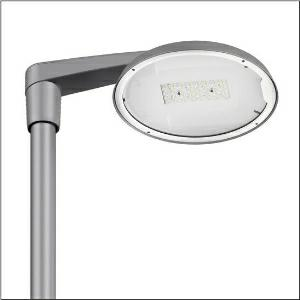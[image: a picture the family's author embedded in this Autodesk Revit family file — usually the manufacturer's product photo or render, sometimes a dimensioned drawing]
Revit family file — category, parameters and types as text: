
# Revit family: dl_r__50_iq_mini___st0_5a_5xa248b41f08je_3ec1
name_source: partatom
category: Lighting Fixtures
units: mm (PartAtom-declared; Revit-internal decimal feet)

## family parameters
Cut with Voids When Loaded = No
Host = Face
Light Source = No
Part Type = Normal
Room Calculation Point = No
Round Connector Dimension = Use Diameter
Shared = No

## types (1)
- --- (1 x LED, 10300 lm, 62.6 W, 4000K)
    Apparent Load = 63 VA
    CIE Flux Codes = 43 76 97 100 100
    Color Rendering = 70
    Color Temperature = 4000K
    Default Elevation = 1800 mm
    Description = DL® 50 iQ mini, mast luminaire, primary light control with lens, of PMMA, primary optical cover: cover, of toughened safety glass, transparent, light distribution: ST0.5a, light emission: direct distribution, primary light characteristic: asymmetric, installation type: side-entry, post-top, LED, High Power LED, rated luminous flux: 10.300lm, luminous efficacy: 165lm/W, light colour: 740, colour temperature: 4000K, control gear: iQ Street-Remote, control: optimised constant luminous flux control (CLO 2.0), Desk-Remote (wireless, voltage-free reading and setting of iQ features in the workshop via application-optimized NFC function/RFID function), Light-Fading, Smart-Wire, Night-Set, Lumen-Switch, Temp-Guard, Auto-Match, Street-Remote, mains connection: 230..240V, AC, 50/60Hz, connection cable pre-assembled, cable length: 8,5m, start of lifetime: 63W, end of service life: 65W, reduction: 29W, luminaire housing, of diecast aluminium, powder-coated, Siteco® metallic grey (DB 702S), inclination adjustable: 0°, 5°, 10° (post-top) | 0°, -5°, -10°, -15° (side-entry), please order mast post-top element or mast side-entry element separately, diameter: 500mm, height: 115mm, post-top: for spigot size d x l = 76 x 100mm; with reducer (optional accessory) 60 x 100mm | side-entry: for spigot size d x l = 60 x 100mm; with reducer (optional accessory) 42 x 100mm, mounting height: 4..6m, protection rating (complete): IP66, insulation class (complete): insulation class II (safety insulation), certification: CE, ENEC, ENEC+, VDE, impact resistance: IK08, permissible operating ambient temperature for outdoor applications: -25..+40°C, standard-compliant lighting for roads and squares, packaging unit: 1 piece

Light Distribution: ST0.5a
    Height = 115 mm
    Lamp = 1 x LED
    Lamp Light Flux = 10300 lm
    Lamp Power = 62.6 W
    Lamp count = 1
    Length = 500 mm
    Luminous efficacy = 165 lm/W
    Manufacturer = Siteco
    ModVariant = No
    Model = 5XA248B41F08JE
    Number of Poles = 1
    OnlyDefault = Yes
    Power Factor = 1
    Product Name = DL® 50 iQ mini | ST0.5a
    Product group = mast luminaire | pylon top
    ProductGroupID = 6100
    Protection Class = Protection class II
    Protection Degree = IP 66
    RLX_Detail_Level = 1
    RLX_Emergency_Light_Flux = 0 lm
    RLX_Emergency_Type = 0
    RLX_Emergency_Type_DB = No
    RlxData = <blob elided: 127329 chars, md5=ab3514f7>
    Socket = socket
    Standby Power = 0 W
    System Light Flux = 10300 lm
    System Power = 63 W
    Type Comments = factory setting: luminous flux: 100 % | dim-lin: 254 | 658 mA
    Type Image = l_1251794.jpg
    URL = http://relux.com
    VarID = @adj_164361
    Voltage = 0 V
    Weight = 0.00 kg
    Width = 0 mm  [stored 0 ft]

note: [stored X ft] marks values corroborated as IEEE doubles in the binary element streams (Revit-internal decimal feet)

## geometry (parser evidence)
native form markers: Blend x4, Sweep x10
no freeform markers — native parametric forms only
